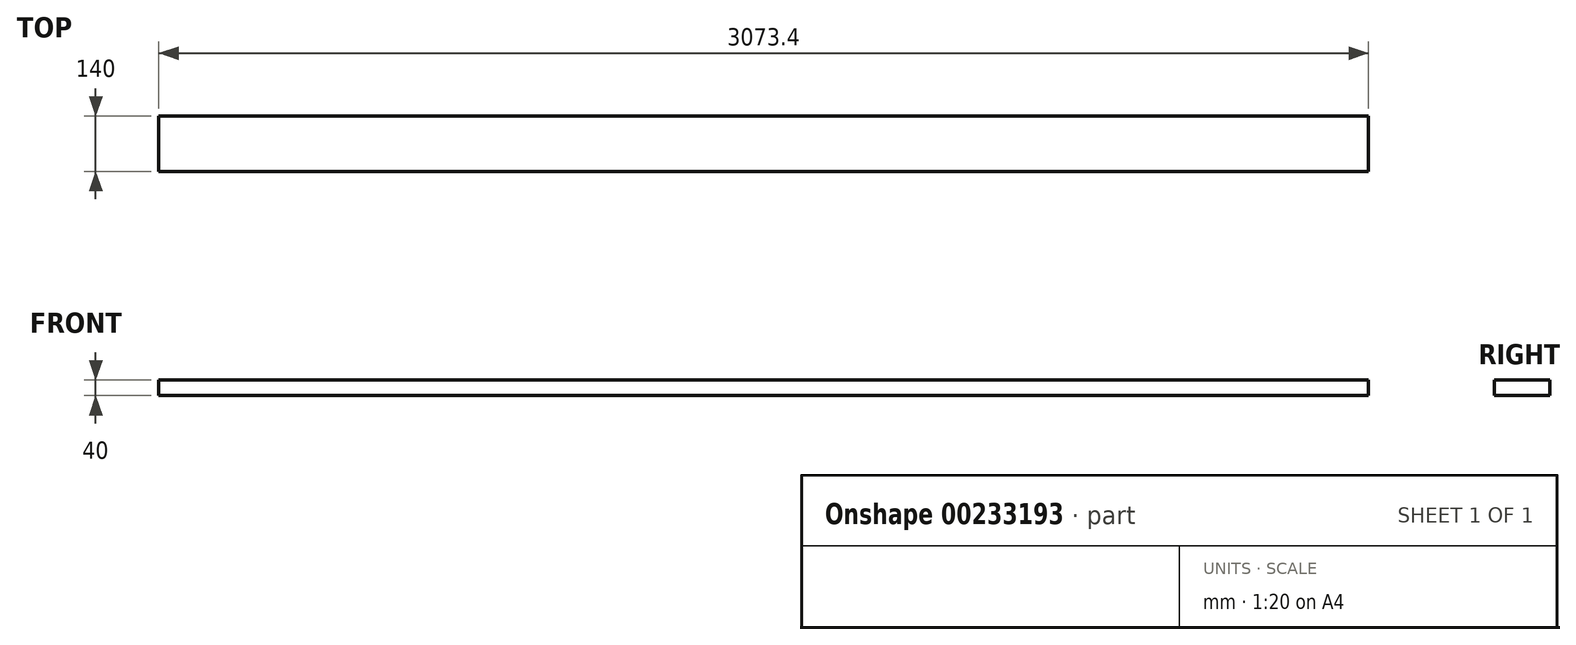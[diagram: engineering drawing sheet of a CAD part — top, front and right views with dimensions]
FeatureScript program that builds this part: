
annotation { "Feature Type Name" : "Feature", "Feature Type Description" : "" }
export const myFeature = defineFeature(function(context is Context, id is Id, definition is map)
    precondition{}
    {
        {
            var Q0;
            Q0=qCreatedBy(makeId("Top.planeOp"),FACE);
            var sketch = newSketch(context, id + "F0", { "sketchPlane" : qUnion([Q0])});
            skLineSegment(sketch, "E0.bottom", {"start": v(-255.04, 140) * mm, "end": v(2818.36, 140) * mm});
            skLineSegment(sketch, "E0.top", {"start": v(-255.04, 0) * mm, "end": v(2818.36, 0) * mm});
            skLineSegment(sketch, "E0.left", {"start": v(-255.04, 140) * mm, "end": v(-255.04, 0) * mm});
            skLineSegment(sketch, "E0.right", {"start": v(2818.36, 140) * mm, "end": v(2818.36, 0) * mm});
            skSolve(sketch);
        }
        {
            var Q0;
            Q0 = qSketchRegion(id + "F0", true);
            extrude(context, id + "F1", {"entities" : qUnion([Q0]), "depth" : 40 * mm});
        }
    });
